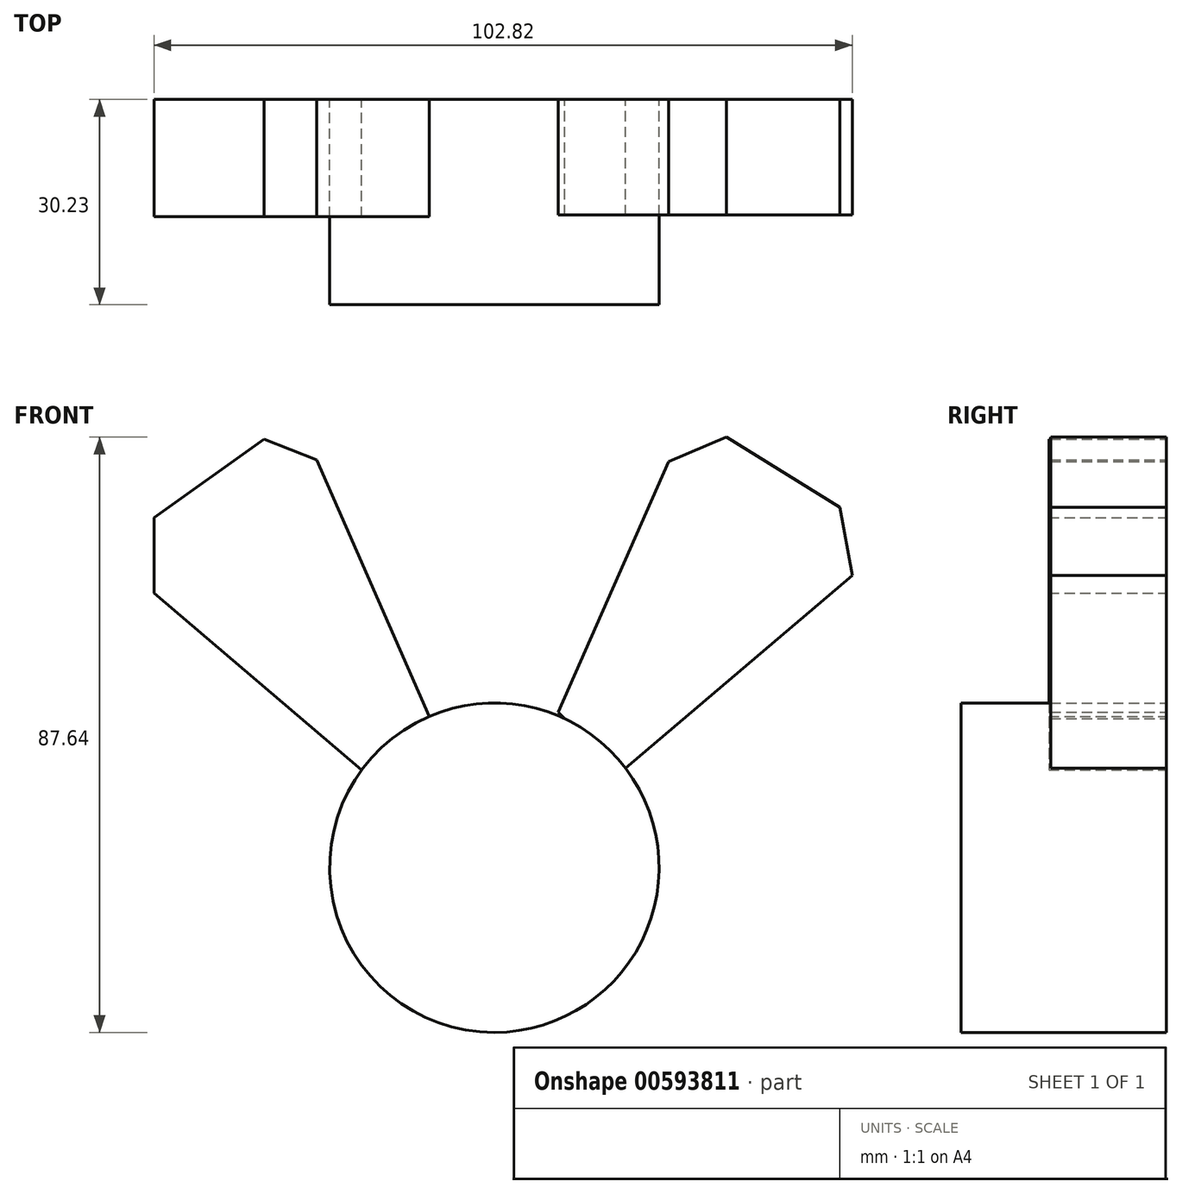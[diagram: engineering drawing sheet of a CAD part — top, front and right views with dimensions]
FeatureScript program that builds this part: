
annotation { "Feature Type Name" : "Feature", "Feature Type Description" : "" }
export const myFeature = defineFeature(function(context is Context, id is Id, definition is map)
    precondition{}
    {
        {
            var Q0;
            Q0=qCreatedBy(makeId("Front.planeOp"),FACE);
            var sketch = newSketch(context, id + "F0", { "sketchPlane" : qUnion([Q0])});
            skCircle(sketch, "E0", {"center": v(0, 0) * mm, "radius": 24.25 * mm});
            skSolve(sketch);
        }
        {
            var Q0;
            Q0=makeQuery(id+"F0.imprint","IMPRINT",FACE,{"disambiguationData":[TD([[makeQuery(id+"F0.imprint","IMPRINT",EDGE,{"derivedFrom":sQuery(id+"F0.wireOp",EDGE,"E0")}),1.0]])]});
            extrude(context, id + "F1", {"entities" : qUnion([Q0]), "depth" : 30.23 * mm, "offsetDistance" : 25.4 * mm});
        }
        {
            var Q0;
            Q0=qCreatedBy(makeId("Front.planeOp"),FACE);
            var sketch = newSketch(context, id + "F2", { "sketchPlane" : qUnion([Q0])});
            skLineSegment(sketch, "E1", {"start": v(-33.89, 63.13) * mm, "end": v(-50.12, 51.54) * mm});
            skLineSegment(sketch, "E2", {"start": v(-50.12, 51.54) * mm, "end": v(-50.12, 40.46) * mm});
            skLineSegment(sketch, "E3", {"start": v(-50.12, 40.46) * mm, "end": v(-18.68, 13.66) * mm});
            skLineSegment(sketch, "E4", {"start": v(-33.89, 63.13) * mm, "end": v(-26.15, 60.04) * mm});
            skLineSegment(sketch, "E5", {"start": v(-26.15, 60.04) * mm, "end": v(-8.89, 20.61) * mm});
            skLineSegment(sketch, "E6", {"start": v(-8.89, 20.61) * mm, "end": v(-18.68, 13.66) * mm});
            skSolve(sketch);
        }
        {
            var Q0;
            Q0=makeQuery(id+"F2.imprint","IMPRINT",FACE,{"disambiguationData":[TD([[makeQuery(id+"F2.imprint","IMPRINT",EDGE,{"derivedFrom":sQuery(id+"F2.wireOp",EDGE,"E1")}),1.0]])]});
            extrude(context, id + "F3", {"entities" : qUnion([Q0]), "operationType" : NewBodyOperationType.ADD, "depth" : 17.27 * mm, "offsetDistance" : 25.4 * mm});
        }
        {
            var Q0;
            Q0=makeQuery(id+"F3.boolean.opBoolean","MERGE",FACE,{"derivedFrom":[makeQuery(id+"F1.opExtrude","CAP_FACE",FACE,{"disambiguationData":[OSD([sQuery(id+"F0.wireOp",EDGE,"E0")])],"isStart":true}),makeQuery(id+"F3.opExtrude","CAP_FACE",FACE,{"disambiguationData":[OSD([sQuery(id+"F2.wireOp",EDGE,"E1"),sQuery(id+"F2.wireOp",EDGE,"E2"),sQuery(id+"F2.wireOp",EDGE,"E3"),sQuery(id+"F2.wireOp",EDGE,"E4"),sQuery(id+"F2.wireOp",EDGE,"E5"),sQuery(id+"F2.wireOp",EDGE,"E6")])],"isStart":true})]});
            extrude(context, id + "F4", {"entities" : qUnion([Q0]), "operationType" : NewBodyOperationType.ADD, "oppositeDirection" : true, "depth" : 12.2 * mm, "offsetDistance" : 25.4 * mm});
        }
        {
            var Q0;
            Q0=qCreatedBy(makeId("Front.planeOp"),FACE);
            var sketch = newSketch(context, id + "F5", { "sketchPlane" : qUnion([Q0])});
            skLineSegment(sketch, "E7", {"start": v(9.4, 22.93) * mm, "end": v(25.64, 59.78) * mm});
            skLineSegment(sketch, "E8", {"start": v(25.64, 59.78) * mm, "end": v(34.14, 63.39) * mm});
            skLineSegment(sketch, "E9", {"start": v(18.17, 13.66) * mm, "end": v(9.4, 22.93) * mm});
            skLineSegment(sketch, "E10", {"start": v(34.14, 63.39) * mm, "end": v(50.9, 53.08) * mm});
            skLineSegment(sketch, "E11", {"start": v(50.9, 53.08) * mm, "end": v(52.7, 43.03) * mm});
            skLineSegment(sketch, "E12", {"start": v(52.7, 43.03) * mm, "end": v(18.17, 13.66) * mm});
            skSolve(sketch);
        }
        {
            var Q0;
            Q0=makeQuery(id+"F5.imprint","IMPRINT",FACE,{"disambiguationData":[TD([[makeQuery(id+"F5.imprint","IMPRINT",EDGE,{"derivedFrom":sQuery(id+"F5.wireOp",EDGE,"E7")}),-1.0]])]});
            extrude(context, id + "F6", {"entities" : qUnion([Q0]), "operationType" : NewBodyOperationType.ADD, "depth" : 17.02 * mm, "offsetDistance" : 25.4 * mm});
        }
    });
